# Revit family: ОВ_К_Р 1
name_source: partatom
category: Mechanical Equipment
units: mm (PartAtom-declared; Revit-internal decimal feet)

## family parameters
Always vertical = Yes
Classification = None
Cut with Voids When Loaded = No
Part Type = Normal
Room Calculation Point = No
Round Connector Dimension = Use Diameter
Shared = No
Work Plane-Based = No

## types (11) — shared parameters
00_20_Виробник = Вентс
00_20_Назва = Осьовий вентилятор низького тиску
Description = Осьовий вентилятор низького тиску у сталевому корпусі для настінного монтажу
Manufacturer = Вентс
URL = https://vents.ua
d1 = 5 mm  [stored 0.0164042 ft]
l = 10 mm  [stored 0.0328084 ft]
t1 = 10 mm  [stored 0.0328084 ft]
Класифікація навантаження = HVAC
Кількість фаз = 1
Матеріал зони обслуговуваня = <By Category>
Напруга = 230 V
Частота = 50 Hz
zero-valued in all types: Default Elevation

## per-type parameters (varying)
- ОВ1 200: B=312 mm; B1=260 mm; D=208 mm; D1=198 mm; D11=193 mm; D111=186 mm; D1_1=63 mm  [stored 0.206693 ft]; D1_11=58 mm  [stored 0.190289 ft]; D2=183 mm; D22=178 mm; D222=213 mm; D2_2=48 mm  [stored 0.15748 ft]; D2_22=43 mm  [stored 0.141076 ft]; D3=168 mm; D33=163 mm; D3_3=33 mm  [stored 0.108268 ft]; D3_33=28 mm  [stored 0.0918635 ft]; D4=153 mm; D44=148 mm; D4_4=18 mm  [stored 0.0590551 ft]; D4_44=13 mm; D5=138 mm; D55=133 mm; D5_5=4 mm  [stored 0.0131234 ft]; D5_55=2 mm  [stored 0.00656168 ft]; D6=123 mm; D66=118 mm; D6_6=9 mm  [stored 0.0295276 ft]; D6_66=8 mm  [stored 0.0262467 ft]; D7=108 mm; D77=103 mm; D7_7=3 mm  [stored 0.00984252 ft]; D7_77=1 mm  [stored 0.00328084 ft]; D8=93 mm; D88=88 mm; D9=78 mm  [stored 0.255906 ft]; D99=73 mm  [stored 0.239501 ft]; Dy=203 mm; E2=119 mm; L=120 mm; d=7 mm  [stored 0.0229659 ft]; l1=104 mm; r=22 mm  [stored 0.0721785 ft]; Вага=3.00 kg; Висота=312 mm; Довжина=120 mm; Діаметр=208 mm; Максимальний потік повітря=405.0 m³/h; Матеріал корпусу=Метал, пофарбований, матовий чорний; Перегородка=Yes; Потужність=43 W; Решетка ОВ1=Yes; Решетка ОВ1 P=No; Решетка ОВК1=No; Рівень звукового тиску на відстані 3 м=33 дБА; Струм=0 A; Установлена потужність=64 VA; Ширина=312 mm
- ОВ1 150: B=250 mm; B1=210 mm; D=162 mm; D1=152 mm; D11=147 mm; D111=186 mm; D1_1=17 mm; D1_11=12 mm  [stored 0.0393701 ft]; D2=137 mm; D22=132 mm; D222=167 mm; D2_2=2 mm  [stored 0.00656168 ft]; D2_22=3 mm  [stored 0.00984252 ft]; D3=122 mm; D33=117 mm; D3_3=6 mm  [stored 0.019685 ft]; D3_33=1 mm  [stored 0.00328084 ft]; D4=107 mm; D44=102 mm; D4_4=7 mm  [stored 0.0229659 ft]; D4_44=7 mm  [stored 0.0229659 ft]; D5=92 mm; D55=87 mm; D5_5=17 mm; D5_55=18 mm  [stored 0.0590551 ft]; D6=77 mm  [stored 0.252625 ft]; D66=72 mm  [stored 0.23622 ft]; D6_6=27 mm  [stored 0.0885827 ft]; D6_66=28 mm  [stored 0.0918635 ft]; D7=62 mm  [stored 0.203412 ft]; D77=57 mm  [stored 0.187008 ft]; D7_7=47 mm  [stored 0.154199 ft]; D7_77=48 mm  [stored 0.15748 ft]; D8=47 mm  [stored 0.154199 ft]; D88=42 mm  [stored 0.137795 ft]; D9=32 mm  [stored 0.104987 ft]; D99=27 mm  [stored 0.0885827 ft]; Dy=157 mm; E2=96 mm; L=120 mm; d=7 mm  [stored 0.0229659 ft]; l1=81 mm  [stored 0.265748 ft]; r=18 mm  [stored 0.0590551 ft]; Вага=2.50 kg; Висота=250 mm; Довжина=120 mm; Діаметр=162 mm; Максимальний потік повітря=200.0 m³/h; Матеріал корпусу=Метал, пофарбований, матовий чорний; Перегородка=Yes; Потужність=36 W; Решетка ОВ1=Yes; Решетка ОВ1 P=No; Решетка ОВК1=No; Рівень звукового тиску на відстані 3 м=33 дБА; Струм=0 A; Установлена потужність=60 VA; Ширина=250 mm
- ОВ1 250: B=370 mm; B1=320 mm; D=262 mm; D1=252 mm; D11=247 mm; D111=186 mm; D1_1=117 mm; D1_11=112 mm; D2=237 mm; D22=232 mm; D222=267 mm; D2_2=102 mm; D2_22=97 mm; D3=222 mm; D33=217 mm; D3_3=87 mm; D3_33=82 mm  [stored 0.269029 ft]; D4=207 mm; D44=202 mm; D4_4=72 mm  [stored 0.23622 ft]; D4_44=67 mm; D5=192 mm; D55=187 mm; D5_5=57 mm  [stored 0.187008 ft]; D5_55=52 mm; D6=177 mm; D66=172 mm; D6_6=42 mm  [stored 0.137795 ft]; D6_66=37 mm  [stored 0.121391 ft]; D7=162 mm; D77=157 mm; D7_7=27 mm  [stored 0.0885827 ft]; D7_77=22 mm  [stored 0.0721785 ft]; D8=147 mm; D88=142 mm; D9=132 mm; D99=127 mm; Dy=257 mm; E2=146 mm; L=140 mm; d=7 mm  [stored 0.0229659 ft]; l1=131 mm; r=26 mm; Вага=3.50 kg; Висота=370 mm; Довжина=140 mm; Діаметр=262 mm; Максимальний потік повітря=1070.0 m³/h; Матеріал корпусу=Метал, пофарбований, матовий чорний; Перегородка=Yes; Потужність=68 W; Решетка ОВ1=Yes; Решетка ОВ1 P=No; Решетка ОВК1=No; Рівень звукового тиску на відстані 3 м=37 дБА; Струм=0 A; Установлена потужність=110 VA; Ширина=370 mm
- ОВ1 315: B=430 mm; B1=380 mm; D=312 mm; D1=302 mm; D11=297 mm; D111=186 mm; D1_1=167 mm; D1_11=162 mm; D2=287 mm; D22=282 mm; D222=317 mm; D2_2=152 mm; D2_22=147 mm; D3=272 mm; D33=267 mm; D3_3=137 mm; D3_33=132 mm; D4=257 mm; D44=252 mm; D4_4=122 mm; D4_44=117 mm; D5=242 mm; D55=237 mm; D5_5=107 mm; D5_55=102 mm; D6=227 mm; D66=222 mm; D6_6=92 mm; D6_66=87 mm; D7=212 mm; D77=207 mm; D7_7=77 mm  [stored 0.252625 ft]; D7_77=72 mm  [stored 0.23622 ft]; D8=197 mm; D88=192 mm; D9=182 mm; D99=177 mm; Dy=307 mm; E2=171 mm; L=170 mm; d=9 mm  [stored 0.0295276 ft]; l1=156 mm; r=30 mm  [stored 0.0984252 ft]; Вага=6.10 kg; Висота=430 mm; Довжина=170 mm; Діаметр=312 mm; Максимальний потік повітря=1700.0 m³/h; Матеріал корпусу=Метал, пофарбований, матовий чорний; Перегородка=Yes; Потужність=110 W; Решетка ОВ1=Yes; Решетка ОВ1 P=No; Решетка ОВК1=No; Рівень звукового тиску на відстані 3 м=42 дБА; Струм=1 A; Установлена потужність=173 VA; Ширина=430 mm
- ОВK1 150: B=250 mm; B1=210 mm; D=162 mm; D1=152 mm; D11=147 mm; D111=190 mm; D1_1=17 mm; D1_11=12 mm  [stored 0.0393701 ft]; D2=137 mm; D22=132 mm; D222=220 mm; D2_2=2 mm  [stored 0.00656168 ft]; D2_22=3 mm  [stored 0.00984252 ft]; D3=122 mm; D33=117 mm; D3_3=6 mm  [stored 0.019685 ft]; D3_33=1 mm  [stored 0.00328084 ft]; D4=107 mm; D44=102 mm; D4_4=7 mm  [stored 0.0229659 ft]; D4_44=7 mm  [stored 0.0229659 ft]; D5=92 mm; D55=87 mm; D5_5=17 mm; D5_55=18 mm  [stored 0.0590551 ft]; D6=77 mm  [stored 0.252625 ft]; D66=72 mm  [stored 0.23622 ft]; D6_6=27 mm  [stored 0.0885827 ft]; D6_66=28 mm  [stored 0.0918635 ft]; D7=62 mm  [stored 0.203412 ft]; D77=57 mm  [stored 0.187008 ft]; D7_7=47 mm  [stored 0.154199 ft]; D7_77=48 mm  [stored 0.15748 ft]; D8=47 mm  [stored 0.154199 ft]; D88=42 mm  [stored 0.137795 ft]; D9=32 mm  [stored 0.104987 ft]; D99=27 mm  [stored 0.0885827 ft]; Dy=157 mm; E2=96 mm; L=120 mm; d=7 mm  [stored 0.0229659 ft]; l1=81 mm  [stored 0.265748 ft]; r=18 mm  [stored 0.0590551 ft]; Вага=2.50 kg; Висота=220 mm; Довжина=120 mm; Діаметр=220 mm; Максимальний потік повітря=200.0 m³/h; Матеріал корпусу=Метал, пофарбований, матовий чорний; Перегородка=Yes; Потужність=36 W; Решетка ОВ1=No; Решетка ОВ1 P=No; Решетка ОВК1=Yes; Рівень звукового тиску на відстані 3 м=33 дБА; Струм=0 A; Установлена потужність=60 VA; Ширина=220 mm
- ОВK1 200: B=312 mm; B1=260 mm; D=208 mm; D1=198 mm; D11=193 mm; D111=270 mm; D1_1=63 mm  [stored 0.206693 ft]; D1_11=58 mm  [stored 0.190289 ft]; D2=183 mm; D22=178 mm; D222=300 mm; D2_2=48 mm  [stored 0.15748 ft]; D2_22=43 mm  [stored 0.141076 ft]; D3=168 mm; D33=163 mm; D3_3=33 mm  [stored 0.108268 ft]; D3_33=28 mm  [stored 0.0918635 ft]; D4=153 mm; D44=148 mm; D4_4=18 mm  [stored 0.0590551 ft]; D4_44=13 mm; D5=138 mm; D55=133 mm; D5_5=4 mm  [stored 0.0131234 ft]; D5_55=2 mm  [stored 0.00656168 ft]; D6=123 mm; D66=118 mm; D6_6=9 mm  [stored 0.0295276 ft]; D6_66=8 mm  [stored 0.0262467 ft]; D7=108 mm; D77=103 mm; D7_7=3 mm  [stored 0.00984252 ft]; D7_77=1 mm  [stored 0.00328084 ft]; D8=93 mm; D88=88 mm; D9=78 mm  [stored 0.255906 ft]; D99=73 mm  [stored 0.239501 ft]; Dy=203 mm; E2=119 mm; L=120 mm; d=7 mm  [stored 0.0229659 ft]; l1=104 mm; r=22 mm  [stored 0.0721785 ft]; Вага=2.50 kg; Висота=300 mm; Довжина=120 mm; Діаметр=300 mm; Максимальний потік повітря=405.0 m³/h; Матеріал корпусу=Метал, пофарбований, матовий чорний; Перегородка=Yes; Потужність=43 W; Решетка ОВ1=No; Решетка ОВ1 P=No; Решетка ОВК1=Yes; Рівень звукового тиску на відстані 3 м=33 дБА; Струм=0 A; Установлена потужність=64 VA; Ширина=300 mm
- ОВK1 250: B=370 mm; B1=320 mm; D=262 mm; D1=252 mm; D11=247 mm; D111=330 mm; D1_1=117 mm; D1_11=112 mm; D2=237 mm; D22=232 mm; D222=360 mm; D2_2=102 mm; D2_22=97 mm; D3=222 mm; D33=217 mm; D3_3=87 mm; D3_33=82 mm  [stored 0.269029 ft]; D4=207 mm; D44=202 mm; D4_4=72 mm  [stored 0.23622 ft]; D4_44=67 mm; D5=192 mm; D55=187 mm; D5_5=57 mm  [stored 0.187008 ft]; D5_55=52 mm; D6=177 mm; D66=172 mm; D6_6=42 mm  [stored 0.137795 ft]; D6_66=37 mm  [stored 0.121391 ft]; D7=162 mm; D77=157 mm; D7_7=27 mm  [stored 0.0885827 ft]; D7_77=22 mm  [stored 0.0721785 ft]; D8=147 mm; D88=142 mm; D9=132 mm; D99=127 mm; Dy=257 mm; E2=146 mm; L=140 mm; d=7 mm  [stored 0.0229659 ft]; l1=131 mm; r=26 mm; Вага=3.00 kg; Висота=360 mm; Довжина=140 mm; Діаметр=360 mm; Максимальний потік повітря=1070.0 m³/h; Матеріал корпусу=Метал, пофарбований, матовий чорний; Перегородка=Yes; Потужність=68 W; Решетка ОВ1=No; Решетка ОВ1 P=No; Решетка ОВК1=Yes; Рівень звукового тиску на відстані 3 м=37 дБА; Струм=0 A; Установлена потужність=110 VA; Ширина=360 mm
- ОВK1 315: B=430 mm; B1=380 mm; D=312 mm; D1=302 mm; D11=297 mm; D111=390 mm; D1_1=167 mm; D1_11=162 mm; D2=287 mm; D22=282 mm; D222=420 mm; D2_2=152 mm; D2_22=147 mm; D3=272 mm; D33=267 mm; D3_3=137 mm; D3_33=132 mm; D4=257 mm; D44=252 mm; D4_4=122 mm; D4_44=117 mm; D5=242 mm; D55=237 mm; D5_5=107 mm; D5_55=102 mm; D6=227 mm; D66=222 mm; D6_6=92 mm; D6_66=87 mm; D7=212 mm; D77=207 mm; D7_7=77 mm  [stored 0.252625 ft]; D7_77=72 mm  [stored 0.23622 ft]; D8=197 mm; D88=192 mm; D9=182 mm; D99=177 mm; Dy=307 mm; E2=171 mm; L=170 mm; d=9 mm  [stored 0.0295276 ft]; l1=156 mm; r=30 mm  [stored 0.0984252 ft]; Вага=5.10 kg; Висота=420 mm; Довжина=170 mm; Діаметр=420 mm; Максимальний потік повітря=1700.0 m³/h; Матеріал корпусу=Метал, пофарбований, матовий чорний; Перегородка=Yes; Потужність=110 W; Решетка ОВ1=No; Решетка ОВ1 P=No; Решетка ОВК1=Yes; Рівень звукового тиску на відстані 3 м=42 дБА; Струм=1 A; Установлена потужність=173 VA; Ширина=420 mm
- ОВ1 150 P: B=325 mm; B1=210 mm; D=162 mm; D1=152 mm; D11=147 mm; D111=190 mm; D1_1=17 mm; D1_11=12 mm  [stored 0.0393701 ft]; D2=137 mm; D22=132 mm; D222=220 mm; D2_2=2 mm  [stored 0.00656168 ft]; D2_22=3 mm  [stored 0.00984252 ft]; D3=122 mm; D33=117 mm; D3_3=6 mm  [stored 0.019685 ft]; D3_33=1 mm  [stored 0.00328084 ft]; D4=107 mm; D44=102 mm; D4_4=7 mm  [stored 0.0229659 ft]; D4_44=7 mm  [stored 0.0229659 ft]; D5=92 mm; D55=87 mm; D5_5=17 mm; D5_55=18 mm  [stored 0.0590551 ft]; D6=77 mm  [stored 0.252625 ft]; D66=72 mm  [stored 0.23622 ft]; D6_6=27 mm  [stored 0.0885827 ft]; D6_66=28 mm  [stored 0.0918635 ft]; D7=62 mm  [stored 0.203412 ft]; D77=57 mm  [stored 0.187008 ft]; D7_7=47 mm  [stored 0.154199 ft]; D7_77=48 mm  [stored 0.15748 ft]; D8=47 mm  [stored 0.154199 ft]; D88=42 mm  [stored 0.137795 ft]; D9=32 mm  [stored 0.104987 ft]; D99=27 mm  [stored 0.0885827 ft]; Dy=157 mm; E2=96 mm; L=127 mm; d=7 mm  [stored 0.0229659 ft]; l1=81 mm  [stored 0.265748 ft]; r=23 mm  [stored 0.0754593 ft]; Вага=2.50 kg; Висота=325 mm; Довжина=127 mm; Діаметр=162 mm; Максимальний потік повітря=200.0 m³/h; Матеріал корпусу=Пластмаса, непрозора, біла; Перегородка=No; Потужність=36 W; Решетка ОВ1=No; Решетка ОВ1 P=Yes; Решетка ОВК1=No; Рівень звукового тиску на відстані 3 м=33 дБА; Струм=0 A; Установлена потужність=60 VA; Ширина=325 mm
- ОВ1 200 P: B=325 mm; B1=210 mm; D=208 mm; D1=198 mm; D11=193 mm; D111=190 mm; D1_1=63 mm  [stored 0.206693 ft]; D1_11=58 mm  [stored 0.190289 ft]; D2=183 mm; D22=178 mm; D222=220 mm; D2_2=48 mm  [stored 0.15748 ft]; D2_22=43 mm  [stored 0.141076 ft]; D3=168 mm; D33=163 mm; D3_3=33 mm  [stored 0.108268 ft]; D3_33=28 mm  [stored 0.0918635 ft]; D4=153 mm; D44=148 mm; D4_4=18 mm  [stored 0.0590551 ft]; D4_44=13 mm; D5=138 mm; D55=133 mm; D5_5=4 mm  [stored 0.0131234 ft]; D5_55=2 mm  [stored 0.00656168 ft]; D6=123 mm; D66=118 mm; D6_6=9 mm  [stored 0.0295276 ft]; D6_66=8 mm  [stored 0.0262467 ft]; D7=108 mm; D77=103 mm; D7_7=3 mm  [stored 0.00984252 ft]; D7_77=1 mm  [stored 0.00328084 ft]; D8=93 mm; D88=88 mm; D9=78 mm  [stored 0.255906 ft]; D99=73 mm  [stored 0.239501 ft]; Dy=203 mm; E2=119 mm; L=127 mm; d=7 mm  [stored 0.0229659 ft]; l1=104 mm; r=23 mm  [stored 0.0754593 ft]; Вага=3.00 kg; Висота=325 mm; Довжина=127 mm; Діаметр=208 mm; Максимальний потік повітря=405.0 m³/h; Матеріал корпусу=Пластмаса, непрозора, біла; Перегородка=No; Потужність=43 W; Решетка ОВ1=No; Решетка ОВ1 P=Yes; Решетка ОВК1=No; Рівень звукового тиску на відстані 3 м=32 дБА; Струм=0 A; Установлена потужність=64 VA; Ширина=325 mm
- ОВ1 250 P: B=325 mm; B1=320 mm; D=262 mm; D1=252 mm; D11=247 mm; D111=186 mm; D1_1=117 mm; D1_11=112 mm; D2=237 mm; D22=232 mm; D222=267 mm; D2_2=102 mm; D2_22=97 mm; D3=222 mm; D33=217 mm; D3_3=87 mm; D3_33=82 mm  [stored 0.269029 ft]; D4=207 mm; D44=202 mm; D4_4=72 mm  [stored 0.23622 ft]; D4_44=67 mm; D5=192 mm; D55=187 mm; D5_5=57 mm  [stored 0.187008 ft]; D5_55=52 mm; D6=177 mm; D66=172 mm; D6_6=42 mm  [stored 0.137795 ft]; D6_66=37 mm  [stored 0.121391 ft]; D7=162 mm; D77=157 mm; D7_7=27 mm  [stored 0.0885827 ft]; D7_77=22 mm  [stored 0.0721785 ft]; D8=147 mm; D88=142 mm; D9=132 mm; D99=127 mm; Dy=257 mm; E2=146 mm; L=152 mm; d=7 mm  [stored 0.0229659 ft]; l1=131 mm; r=23 mm  [stored 0.0754593 ft]; Вага=3.50 kg; Висота=325 mm; Довжина=152 mm; Діаметр=262 mm; Максимальний потік повітря=1070.0 m³/h; Матеріал корпусу=Пластмаса, непрозора, біла; Перегородка=No; Потужність=68 W; Решетка ОВ1=No; Решетка ОВ1 P=Yes; Решетка ОВК1=No; Рівень звукового тиску на відстані 3 м=37 дБА; Струм=0 A; Установлена потужність=110 VA; Ширина=325 mm

note: column(s) folded — value = type name in every type: 00_20_Тип

note: [stored X ft] marks values corroborated as IEEE doubles in the binary element streams (Revit-internal decimal feet)
